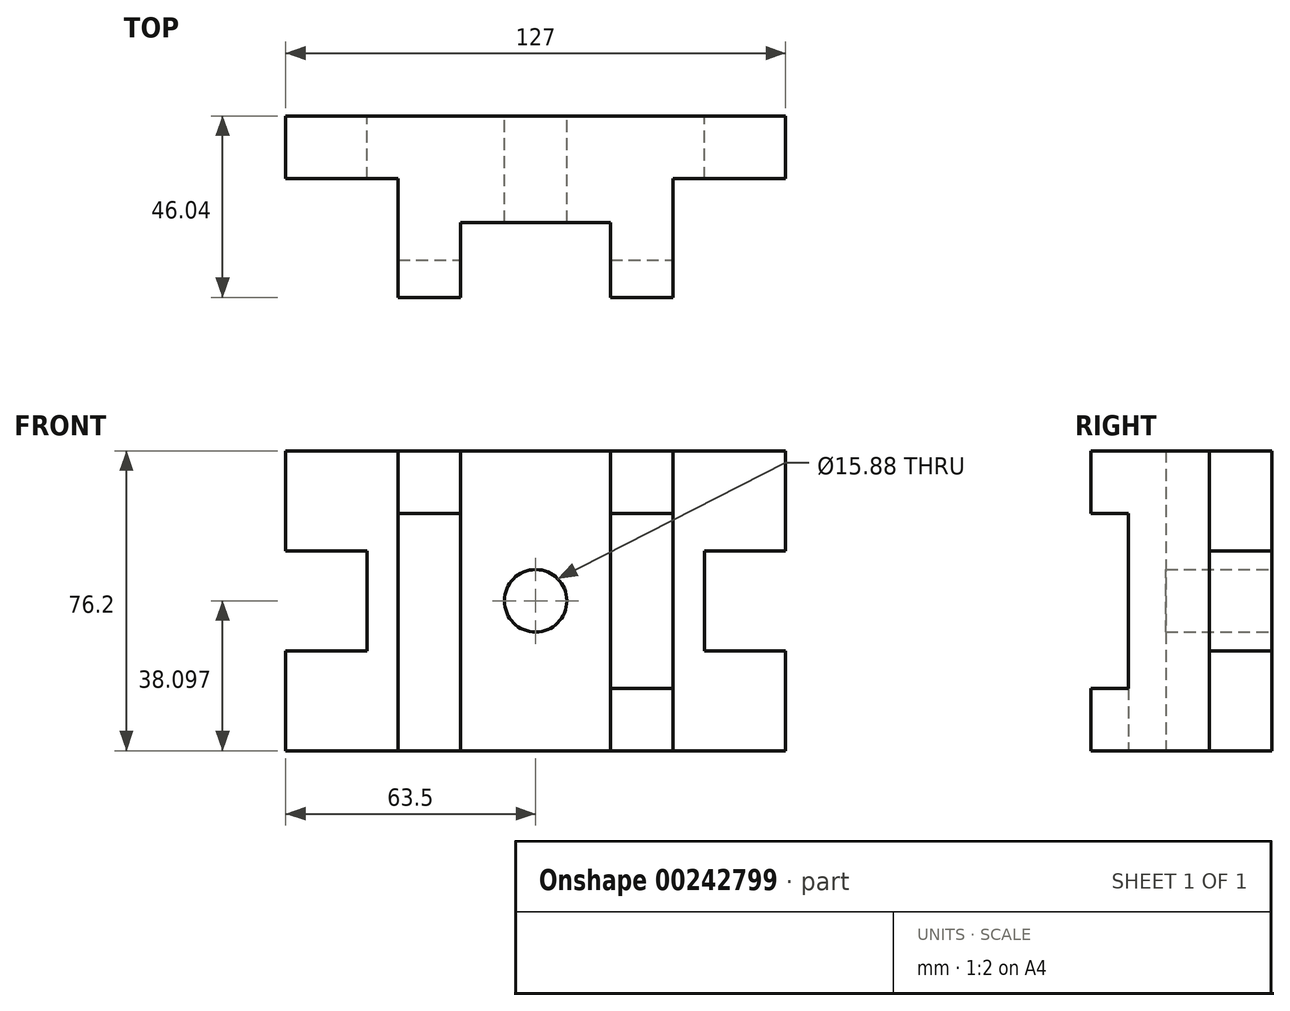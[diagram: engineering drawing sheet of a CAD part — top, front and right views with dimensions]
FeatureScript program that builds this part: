
annotation { "Feature Type Name" : "Feature", "Feature Type Description" : "" }
export const myFeature = defineFeature(function(context is Context, id is Id, definition is map)
    precondition{}
    {
        {
            var Q0;
            Q0=qCreatedBy(makeId("Front.planeOp"),FACE);
            var sketch = newSketch(context, id + "F0", { "sketchPlane" : qUnion([Q0])});
            skLineSegment(sketch, "E0", {"start": v(-127, 84.1) * mm, "end": v(-127, 33.3) * mm});
            skLineSegment(sketch, "E1", {"start": v(-127, -68.3) * mm, "end": v(127, -68.3) * mm});
            skLineSegment(sketch, "E2", {"start": v(127, -68.3) * mm, "end": v(127, -17.5) * mm});
            skLineSegment(sketch, "E3", {"start": v(-127, 84.1) * mm, "end": v(127, 84.1) * mm});
            skLineSegment(sketch, "E4", {"start": v(-127, -17.5) * mm, "end": v(-85.72, -17.5) * mm});
            skLineSegment(sketch, "E5", {"start": v(-127, 33.3) * mm, "end": v(-85.73, 33.3) * mm});
            skLineSegment(sketch, "E6", {"start": v(-127, -17.5) * mm, "end": v(-127, -68.3) * mm});
            skLineSegment(sketch, "E7", {"start": v(-85.72, 33.3) * mm, "end": v(-85.72, -17.5) * mm});
            skLineSegment(sketch, "E8.MirrorCS", {"start": v(127, 33.3) * mm, "end": v(85.73, 33.3) * mm});
            skLineSegment(sketch, "E9.MirrorCS", {"start": v(85.72, 33.3) * mm, "end": v(85.72, -17.5) * mm});
            skLineSegment(sketch, "E10.MirrorCS", {"start": v(127, -17.5) * mm, "end": v(85.72, -17.5) * mm});
            skLineSegment(sketch, "E11.trimOffspring", {"start": v(127, 33.3) * mm, "end": v(127, 84.1) * mm});
            skLineSegment(sketch, "E12", {"start": v(-127, 84.1) * mm, "end": v(-69.85, 84.1) * mm});
            skLineSegment(sketch, "E13", {"start": v(-69.85, 84.1) * mm, "end": v(-69.85, -68.3) * mm});
            skLineSegment(sketch, "E14.MirrorCS", {"start": v(69.85, 84.1) * mm, "end": v(69.85, -68.3) * mm});
            skLineSegment(sketch, "E15", {"start": v(-38.1, 84.1) * mm, "end": v(-38.1, -68.3) * mm});
            skLineSegment(sketch, "E16", {"start": v(-69.85, -68.3) * mm, "end": v(-38.1, -68.3) * mm});
            skLineSegment(sketch, "E17.MirrorCS", {"start": v(38.1, 84.1) * mm, "end": v(38.1, -68.3) * mm});
            skLineSegment(sketch, "E18", {"start": v(-69.85, 52.35) * mm, "end": v(-38.1, 52.35) * mm});
            skLineSegment(sketch, "E19", {"start": v(-38.1, 52.35) * mm, "end": v(-38.1, 84.1) * mm});
            skLineSegment(sketch, "E20", {"start": v(-38.1, -36.55) * mm, "end": v(-69.85, -36.55) * mm});
            skLineSegment(sketch, "E21", {"start": v(-69.85, -36.55) * mm, "end": v(-69.85, -68.3) * mm});
            skLineSegment(sketch, "E22", {"start": v(-69.85, -36.55) * mm, "end": v(-38.1, -36.55) * mm});
            skLineSegment(sketch, "E23", {"start": v(-69.85, -68.3) * mm, "end": v(-69.85, -36.55) * mm});
            skLineSegment(sketch, "E24", {"start": v(-38.1, -36.55) * mm, "end": v(-38.1, -68.3) * mm});
            skLineSegment(sketch, "E25.MirrorCS", {"start": v(69.85, 52.35) * mm, "end": v(38.1, 52.35) * mm});
            skLineSegment(sketch, "E26.MirrorCS", {"start": v(38.1, -36.55) * mm, "end": v(69.85, -36.55) * mm});
            skPoint(sketch, "E27.orphan", {"position": v(0, 131.97) * mm});
            skLineSegment(sketch, "E28", {"start": v(0, 0) * mm, "end": v(0, 15.88) * mm});
            skLineSegment(sketch, "E29", {"start": v(0, 0) * mm, "end": v(0, 84.1) * mm});
            skLineSegment(sketch, "E30", {"start": v(0, 0) * mm, "end": v(0, -15.88) * mm});
            skPoint(sketch, "E31.orphan", {"position": v(0, -68.3) * mm});
            skLineSegment(sketch, "E32", {"start": v(-127, 84.1) * mm, "end": v(0, 84.1) * mm});
            skCircle(sketch, "E33", {"center": v(0, 7.9) * mm, "radius": 15.88 * mm});
            skLineSegment(sketch, "E34", {"start": v(0, 7.9) * mm, "end": v(0, -68.3) * mm});
            skPoint(sketch, "E35.orphan", {"position": v(-85.72, 7.9) * mm});
            skPoint(sketch, "E36.trimOffspring.end.orphan", {"position": v(85.72, 7.9) * mm});
            skSolve(sketch);
        }
        {
            var Q0;
            Q0 = qSketchRegion(id + "F0", true);
            extrude(context, id + "F1", {"entities" : qUnion([Q0]), "depth" : 31.75 * mm});
        }
        {
            var Q0;
            {var subQ4=sQuery(id+"F0.wireOp",EDGE,"E18");Q0=makeQuery(id+"F0.imprint","IMPRINT",FACE,{"disambiguationData":[TD([[makeQuery(id+"F0.imprint","IMPRINT",EDGE,{"derivedFrom":subQ4}),1.0]])]});}
            var Q1;
            Q1=makeQuery(id+"F0.imprint","IMPRINT",FACE,{"disambiguationData":[TD([[makeQuery(id+"F0.imprint","IMPRINT",EDGE,{"derivedFrom":sQuery(id+"F0.wireOp",EDGE,"E23")}),-1.0]])]});
            var Q2;
            {var subQ5=sQuery(id+"F0.wireOp",EDGE,"E26.MirrorCS");Q2=makeQuery(id+"F0.imprint","IMPRINT",FACE,{"disambiguationData":[TD([[makeQuery(id+"F0.imprint","IMPRINT",EDGE,{"derivedFrom":subQ5}),-1.0]])]});}
            var Q3;
            {var subQ5=sQuery(id+"F0.wireOp",EDGE,"E25.MirrorCS");Q3=makeQuery(id+"F0.imprint","IMPRINT",FACE,{"disambiguationData":[TD([[makeQuery(id+"F0.imprint","IMPRINT",EDGE,{"derivedFrom":subQ5}),-1.0]])]});}
            extrude(context, id + "F2", {"entities" : qUnion([Q0, Q1, Q2, Q3]), "operationType" : NewBodyOperationType.ADD, "depth" : 92.07 * mm});
        }
        {
            var Q0;
            Q0=makeQuery(id+"F0.imprint","IMPRINT",FACE,{"disambiguationData":[TD([[makeQuery(id+"F0.imprint","IMPRINT",EDGE,{"derivedFrom":sQuery(id+"F0.wireOp",EDGE,"E15")}),1.0]])]});
            var Q1;
            {var subQ4=sQuery(id+"F0.wireOp",EDGE,"E17.MirrorCS");var subQ9=sQuery(id+"F0.wireOp",EDGE,"E1");var subQ10=makeQuery(id+"F0.imprint","INTERSECT",VERTEX,{"derivedFrom":[subQ9,subQ4]});Q1=makeQuery(id+"F0.imprint","IMPRINT",FACE,{"disambiguationData":[TD([[makeQuery(id+"F0.imprint","IMPRINT",EDGE,{"disambiguationData":[TD([[subQ10,1.0]])],"derivedFrom":subQ9}),1.0]])]});}
            extrude(context, id + "F3", {"entities" : qUnion([Q0, Q1]), "operationType" : NewBodyOperationType.ADD, "depth" : 53.97 * mm});
        }
        {
            var Q0;
            Q0=makeQuery(id+"F0.imprint","IMPRINT",FACE,{"disambiguationData":[TD([[makeQuery(id+"F0.imprint","IMPRINT",EDGE,{"derivedFrom":sQuery(id+"F0.wireOp",EDGE,"E15")}),-1.0]])]});
            var Q1;
            {var subQ0=sQuery(id+"F0.wireOp",EDGE,"E25.MirrorCS");Q1=makeQuery(id+"F0.imprint","IMPRINT",FACE,{"disambiguationData":[TD([[makeQuery(id+"F0.imprint","IMPRINT",EDGE,{"derivedFrom":subQ0}),1.0]])]});}
            extrude(context, id + "F4", {"entities" : qUnion([Q0, Q1]), "operationType" : NewBodyOperationType.ADD, "depth" : 73.02 * mm});
        }
        {
            var Q0;
            Q0=makeQuery(id+"F1.opExtrude","SWEPT_BODY",BODY,{"disambiguationData":[OSD([sQuery(id+"F0.wireOp",EDGE,"E1"),sQuery(id+"F0.wireOp",EDGE,"E2"),sQuery(id+"F0.wireOp",EDGE,"E3"),sQuery(id+"F0.wireOp",EDGE,"E4"),sQuery(id+"F0.wireOp",EDGE,"E5"),sQuery(id+"F0.wireOp",EDGE,"E0"),sQuery(id+"F0.wireOp",EDGE,"E7"),sQuery(id+"F0.wireOp",EDGE,"E6"),sQuery(id+"F0.wireOp",EDGE,"E8.MirrorCS"),sQuery(id+"F0.wireOp",EDGE,"E9.MirrorCS"),sQuery(id+"F0.wireOp",EDGE,"E10.MirrorCS"),sQuery(id+"F0.wireOp",EDGE,"E11.trimOffspring"),sQuery(id+"F0.wireOp",EDGE,"BH3tLkia-Ak3l-O7Nb-EvXt-rNK0TBWOUVO7"),sQuery(id+"F0.wireOp",EDGE,"E12"),sQuery(id+"F0.wireOp",EDGE,"E13"),sQuery(id+"F0.wireOp",EDGE,"E14.MirrorCS"),sQuery(id+"F0.wireOp",EDGE,"E15"),sQuery(id+"F0.wireOp",EDGE,"E17.MirrorCS"),sQuery(id+"F0.wireOp",EDGE,"E18"),sQuery(id+"F0.wireOp",EDGE,"E16"),sQuery(id+"F0.wireOp",EDGE,"E20"),sQuery(id+"F0.wireOp",EDGE,"E25.MirrorCS"),sQuery(id+"F0.wireOp",EDGE,"E26.MirrorCS")])]});
            var Q1;
            Q1=makeQuery(id+"F1.opExtrude","CAP_VERTEX",VERTEX,{"disambiguationData":[OSD([sQuery(id+"F0.wireOp",EDGE,"E0"),sQuery(id+"F0.wireOp",EDGE,"E32")])],"isStart":false});
            transform(context, id + "F5", {"entities" : qUnion([Q0]), "transformType" : TransformType.SCALE_UNIFORMLY, "scale" : 0.5, "scalePoint" : qUnion([Q1]), "makeCopy" : false});
        }
    });
